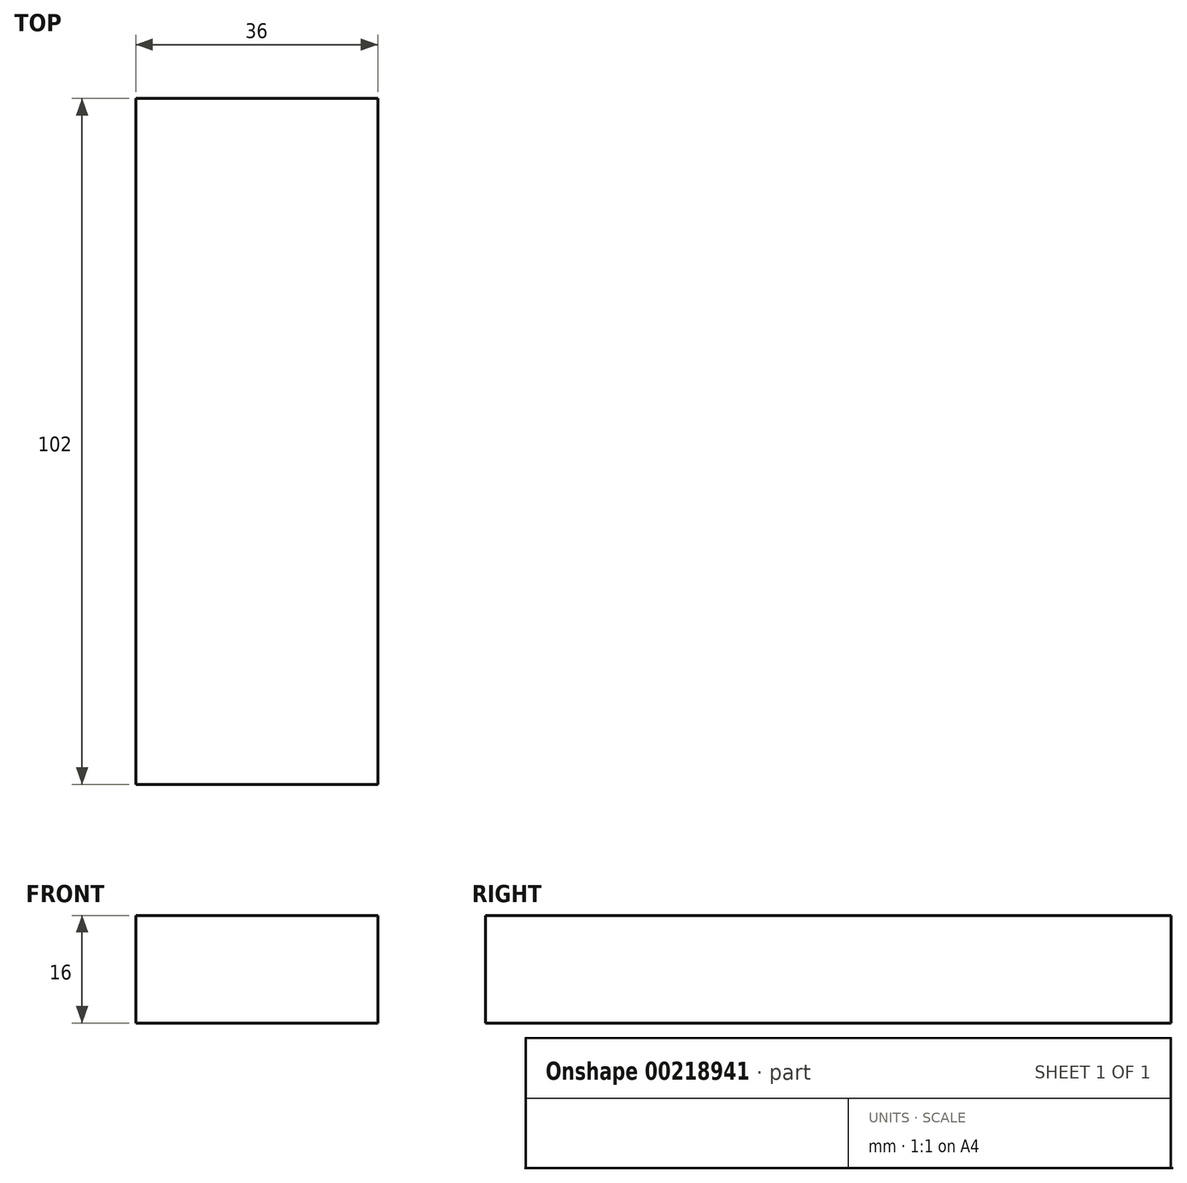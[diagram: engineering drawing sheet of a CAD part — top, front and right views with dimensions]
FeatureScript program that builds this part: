
annotation { "Feature Type Name" : "Feature", "Feature Type Description" : "" }
export const myFeature = defineFeature(function(context is Context, id is Id, definition is map)
    precondition{}
    {
        {
            var Q0;
            Q0=qCreatedBy(makeId("Front.planeOp"),FACE);
            var sketch = newSketch(context, id + "F0", { "sketchPlane" : qUnion([Q0])});
            skLineSegment(sketch, "E0.bottom", {"start": v(18, -8) * mm, "end": v(-18, -8) * mm});
            skLineSegment(sketch, "E0.top", {"start": v(18, 8) * mm, "end": v(-18, 8) * mm});
            skLineSegment(sketch, "E0.left", {"start": v(18, -8) * mm, "end": v(18, 8) * mm});
            skLineSegment(sketch, "E0.right", {"start": v(-18, -8) * mm, "end": v(-18, 8) * mm});
            skPoint(sketch, "E0.middle", {"position": v(0, 0) * mm});
            skSolve(sketch);
        }
        {
            var Q0;
            Q0=makeQuery(id+"F0.imprint","IMPRINT",FACE,{"disambiguationData":[TD([[makeQuery(id+"F0.imprint","IMPRINT",EDGE,{"derivedFrom":sQuery(id+"F0.wireOp",EDGE,"E0.bottom")}),-1.0]])]});
            extrude(context, id + "F1", {"entities" : qUnion([Q0]), "oppositeDirection" : true, "depth" : 102 * mm});
        }
    });
